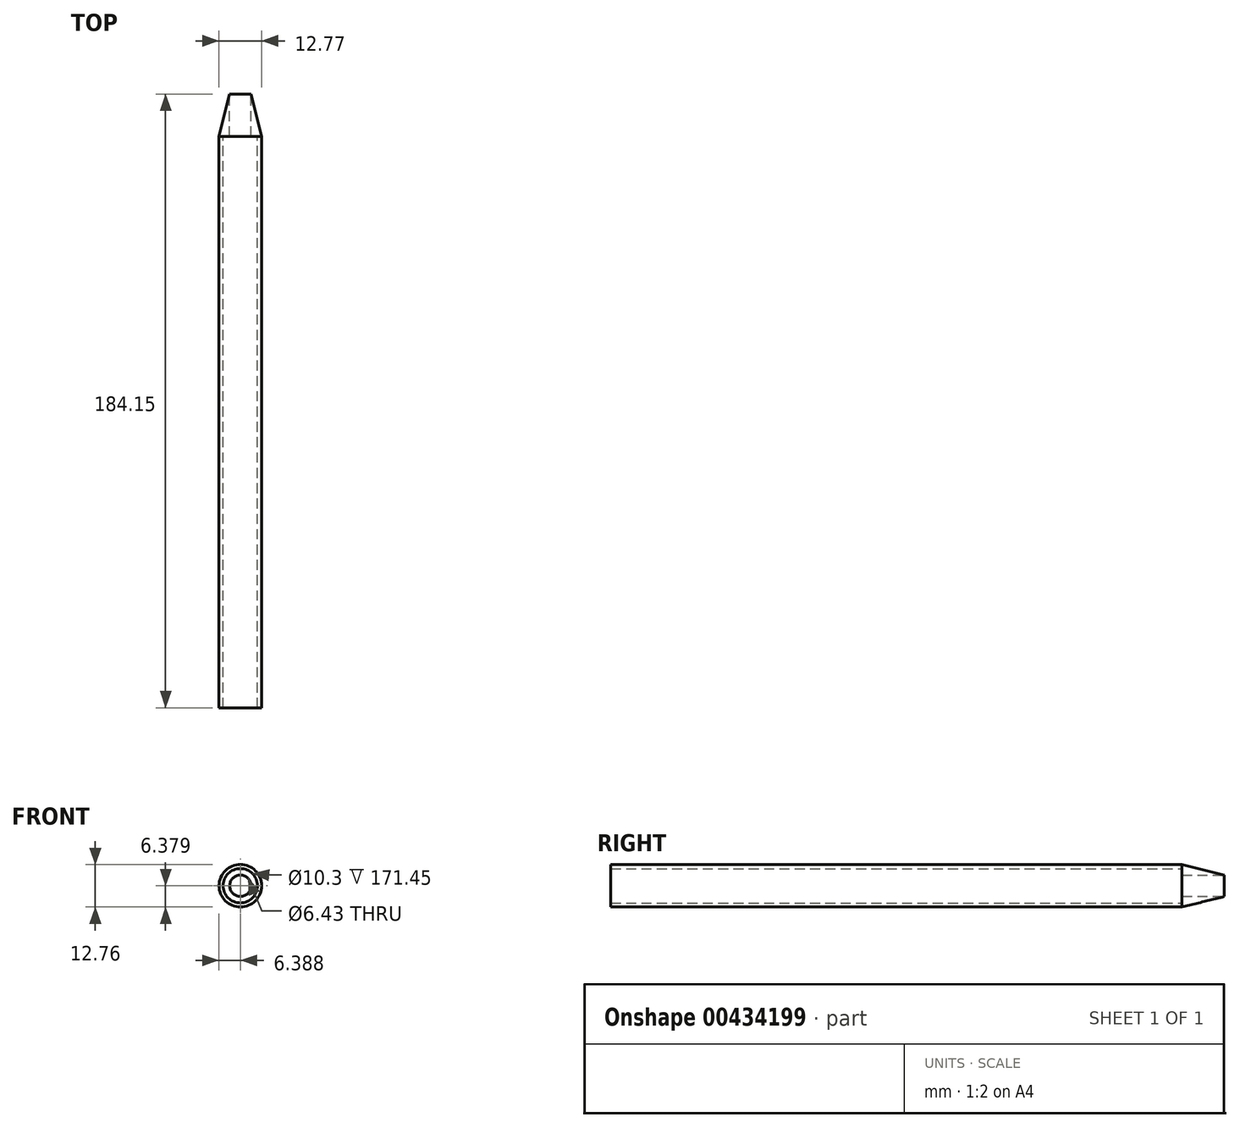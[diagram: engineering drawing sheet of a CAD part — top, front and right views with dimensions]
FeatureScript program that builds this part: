
annotation { "Feature Type Name" : "Feature", "Feature Type Description" : "" }
export const myFeature = defineFeature(function(context is Context, id is Id, definition is map)
    precondition{}
    {
        {
            var Q0;
            Q0=qCreatedBy(makeId("Front.planeOp"),FACE);
            var sketch = newSketch(context, id + "F0", { "sketchPlane" : qUnion([Q0])});
            skCircle(sketch, "E0", {"center": v(-119.91, -45.2) * mm, "radius": 6.38 * mm});
            skSolve(sketch);
        }
        {
            var Q0;
            Q0=makeQuery(id+"F0.imprint","IMPRINT",FACE,{"disambiguationData":[TD([[makeQuery(id+"F0.imprint","IMPRINT",EDGE,{"derivedFrom":sQuery(id+"F0.wireOp",EDGE,"E0")}),1.0]])]});
            var Q1;
            Q1=sQuery(id+"F0.wireOp",EDGE,"E0");
            extrude(context, id + "F1", {"entities" : qUnion([Q0]), "surfaceEntities" : qUnion([Q1]), "depth" : 171.45 * mm});
        }
        {
            var Q0;
            Q0=qCreatedBy(makeId("Front.planeOp"),FACE);
            var sketch = newSketch(context, id + "F2", { "sketchPlane" : qUnion([Q0])});
            skCircle(sketch, "E1", {"center": v(-90.98, -15.66) * mm, "radius": 7.17 * mm});
            skSolve(sketch);
        }
        {
            var Q0;
            Q0=makeQuery(id+"F2.imprint","IMPRINT",FACE,{"disambiguationData":[TD([[makeQuery(id+"F2.imprint","IMPRINT",EDGE,{"derivedFrom":sQuery(id+"F2.wireOp",EDGE,"E1")}),1.0]])]});
            var Q1;
            Q1=sQuery(id+"F2.wireOp",EDGE,"E1");
            extrude(context, id + "F3", {"entities" : qUnion([Q0]), "bodyType" : ToolBodyType.SURFACE, "surfaceEntities" : qUnion([Q1]), "depth" : 31.75 * mm});
        }
        {
            var Q0;
            Q0=qCreatedBy(makeId("Front.planeOp"),FACE);
            var sketch = newSketch(context, id + "F4", { "sketchPlane" : qUnion([Q0])});
            skCircle(sketch, "E2", {"center": v(-119.91, -45.2) * mm, "radius": 5.15 * mm});
            skSolve(sketch);
        }
        {
            var Q0;
            Q0=makeQuery(id+"F4.imprint","IMPRINT",FACE,{"disambiguationData":[TD([[makeQuery(id+"F4.imprint","IMPRINT",EDGE,{"derivedFrom":sQuery(id+"F4.wireOp",EDGE,"E2")}),1.0]])]});
            extrude(context, id + "F5", {"entities" : qUnion([Q0]), "operationType" : NewBodyOperationType.REMOVE, "depth" : 171.45 * mm});
        }
        {
            var Q0;
            Q0=makeQuery(id+"F0.imprint","IMPRINT",FACE,{"disambiguationData":[TD([[makeQuery(id+"F0.imprint","IMPRINT",EDGE,{"derivedFrom":sQuery(id+"F0.wireOp",EDGE,"E0")}),1.0]])]});
            extrude(context, id + "F6", {"entities" : qUnion([Q0]), "operationType" : NewBodyOperationType.ADD, "oppositeDirection" : true, "depth" : 12.7 * mm, "hasDraft" : true, "draftAngle" : 14 * degree, "draftPullDirection" : true});
        }
        {
            var Q0;
            Q0=qCreatedBy(makeId("Front.planeOp"),FACE);
            var sketch = newSketch(context, id + "F7", { "sketchPlane" : qUnion([Q0])});
            skCircle(sketch, "E3", {"center": v(-119.91, -45.2) * mm, "radius": 2.75 * mm});
            skSolve(sketch);
        }
        {
            var Q0;
            Q0=makeQuery(id+"F6.opExtrude","CAP_FACE",FACE,{"disambiguationData":[OSD([sQuery(id+"F0.wireOp",EDGE,"E0")])],"isStart":false});
            var Q1;
            Q1=sQuery(id+"F7.wireOp",EDGE,"E3");
            extrude(context, id + "F8", {"entities" : qUnion([Q0]), "operationType" : NewBodyOperationType.REMOVE, "surfaceEntities" : qUnion([Q1]), "oppositeDirection" : true, "depth" : 25.65 * mm});
        }
    });
